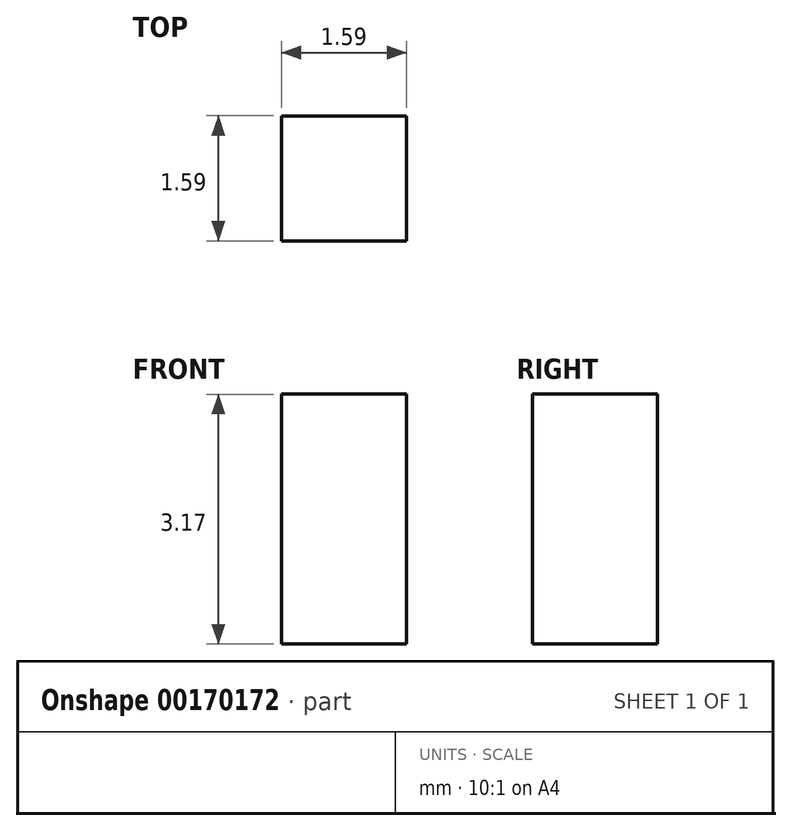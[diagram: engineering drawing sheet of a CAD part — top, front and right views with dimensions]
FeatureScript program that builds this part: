
annotation { "Feature Type Name" : "Feature", "Feature Type Description" : "" }
export const myFeature = defineFeature(function(context is Context, id is Id, definition is map)
    precondition{}
    {
        {
            var Q0;
            Q0=qCreatedBy(makeId("Top.planeOp"),FACE);
            var sketch = newSketch(context, id + "F0", { "sketchPlane" : qUnion([Q0])});
            skCircle(sketch, "E0.cCircle", {"center": v(0, 0) * mm, "radius": 29.07 * mm, "construction": true});
            skLineSegment(sketch, "E0.0", {"start": v(44.45, -29.08) * mm, "end": v(0, -29.07) * mm});
            skLineSegment(sketch, "E0.1", {"start": v(-44.45, -29.06) * mm, "end": v(0, 72.53) * mm});
            skLineSegment(sketch, "E0.2", {"start": v(0, 72.53) * mm, "end": v(44.45, -29.08) * mm});
            skPoint(sketch, "E0.0.midPoint", {"position": v(0, -29.07) * mm});
            skLineSegment(sketch, "E1.0", {"start": v(0, 50.35) * mm, "end": v(30.86, -20.19) * mm});
            skLineSegment(sketch, "E1.1", {"start": v(-30.86, -20.18) * mm, "end": v(0, 50.35) * mm});
            skLineSegment(sketch, "E1.2", {"start": v(30.86, -20.19) * mm, "end": v(-30.86, -20.18) * mm});
            skLineSegment(sketch, "E2", {"start": v(0, 14.54) * mm, "end": v(0, -29.07) * mm});
            skCircle(sketch, "E3", {"center": v(0, -24.63) * mm, "radius": 1.84 * mm});
            skLineSegment(sketch, "E4.bottom", {"start": v(-1.59, -20.18) * mm, "end": v(1.59, -20.18) * mm});
            skLineSegment(sketch, "E4.top", {"start": v(-1.59, -21.77) * mm, "end": v(1.59, -21.77) * mm});
            skLineSegment(sketch, "E4.left", {"start": v(-1.59, -20.18) * mm, "end": v(-1.59, -21.77) * mm});
            skLineSegment(sketch, "E4.right", {"start": v(1.59, -20.18) * mm, "end": v(1.59, -21.77) * mm});
            skLineSegment(sketch, "E5.top", {"start": v(-1.59, -27.48) * mm, "end": v(1.59, -27.48) * mm});
            skLineSegment(sketch, "E5.left", {"start": v(-1.59, -29.07) * mm, "end": v(-1.59, -27.48) * mm});
            skPoint(sketch, "E6", {"position": v(17.59, 10.15) * mm});
            skLineSegment(sketch, "E7.1.0", {"start": v(18.27, 8.72) * mm, "end": v(19.65, 9.5) * mm});
            skLineSegment(sketch, "E7.1.1", {"start": v(19.65, 9.5) * mm, "end": v(18.06, 12.26) * mm});
            skLineSegment(sketch, "E7.1.2", {"start": v(16.95, 11.62) * mm, "end": v(18.06, 12.26) * mm});
            skCircle(sketch, "E7.1.3", {"center": v(21.33, 12.31) * mm, "radius": 1.84 * mm});
            skLineSegment(sketch, "E7.1.4", {"start": v(24.6, 12.37) * mm, "end": v(23, 15.12) * mm});
            skLineSegment(sketch, "E7.1.5", {"start": v(25.97, 13.16) * mm, "end": v(24.6, 12.37) * mm});
            skLineSegment(sketch, "E7.1.6", {"start": v(24.38, 15.91) * mm, "end": v(23, 15.12) * mm});
            skLineSegment(sketch, "E7.1.7", {"start": v(25.97, 13.16) * mm, "end": v(24.38, 15.91) * mm});
            skLineSegment(sketch, "E7.1.8", {"start": v(18.27, 8.72) * mm, "end": v(18.04, 9.11) * mm});
            skLineSegment(sketch, "E7.2.0", {"start": v(-16.95, 11.62) * mm, "end": v(-18.06, 12.26) * mm});
            skLineSegment(sketch, "E7.2.1", {"start": v(-18.06, 12.26) * mm, "end": v(-19.65, 9.5) * mm});
            skLineSegment(sketch, "E7.2.2", {"start": v(-18.27, 8.72) * mm, "end": v(-19.65, 9.5) * mm});
            skCircle(sketch, "E7.2.3", {"center": v(-21.33, 12.31) * mm, "radius": 1.84 * mm});
            skLineSegment(sketch, "E7.2.4", {"start": v(-23, 15.12) * mm, "end": v(-24.6, 12.37) * mm});
            skLineSegment(sketch, "E7.2.5", {"start": v(-24.38, 15.91) * mm, "end": v(-23, 15.12) * mm});
            skLineSegment(sketch, "E7.2.6", {"start": v(-25.97, 13.16) * mm, "end": v(-24.6, 12.37) * mm});
            skLineSegment(sketch, "E7.2.7", {"start": v(-24.38, 15.91) * mm, "end": v(-25.97, 13.16) * mm});
            skLineSegment(sketch, "E7.2.8", {"start": v(-18.04, 9.12) * mm, "end": v(-18.27, 8.72) * mm});
            skCircle(sketch, "E8", {"center": v(0, 55.96) * mm, "radius": 1.84 * mm});
            skLineSegment(sketch, "E9.bottom", {"start": v(-1.59, 60.4) * mm, "end": v(1.59, 60.4) * mm});
            skLineSegment(sketch, "E9.top", {"start": v(-1.59, 58.81) * mm, "end": v(1.59, 58.81) * mm});
            skLineSegment(sketch, "E9.left", {"start": v(-1.59, 60.4) * mm, "end": v(-1.59, 58.81) * mm});
            skLineSegment(sketch, "E10.top", {"start": v(-1.59, 53.1) * mm, "end": v(1.59, 53.1) * mm});
            skLineSegment(sketch, "E10.left", {"start": v(-1.59, 51.51) * mm, "end": v(-1.59, 53.1) * mm});
            skLineSegment(sketch, "E10.right", {"start": v(1.59, 51.51) * mm, "end": v(1.59, 53.1) * mm});
            skLineSegment(sketch, "E11", {"start": v(1.59, 60.4) * mm, "end": v(1.59, 58.81) * mm});
            skLineSegment(sketch, "E12", {"start": v(-1.59, 51.51) * mm, "end": v(1.59, 51.51) * mm});
            skLineSegment(sketch, "E13.1.0", {"start": v(-14.02, 33.37) * mm, "end": v(-12.64, 34.16) * mm});
            skLineSegment(sketch, "E13.1.1", {"start": v(-12.64, 34.16) * mm, "end": v(-14.23, 36.91) * mm});
            skLineSegment(sketch, "E13.1.2", {"start": v(-15.6, 36.12) * mm, "end": v(-14.23, 36.91) * mm});
            skLineSegment(sketch, "E13.1.3", {"start": v(-14.02, 33.37) * mm, "end": v(-15.6, 36.12) * mm});
            skCircle(sketch, "E13.1.4", {"center": v(-10.96, 36.97) * mm, "radius": 1.84 * mm});
            skLineSegment(sketch, "E13.1.5", {"start": v(-7.7, 37.02) * mm, "end": v(-9.28, 39.77) * mm});
            skLineSegment(sketch, "E13.1.6", {"start": v(-6.32, 37.81) * mm, "end": v(-7.9, 40.56) * mm});
            skLineSegment(sketch, "E13.1.7", {"start": v(-6.32, 37.81) * mm, "end": v(-7.7, 37.02) * mm});
            skLineSegment(sketch, "E13.1.8", {"start": v(-7.9, 40.56) * mm, "end": v(-9.28, 39.77) * mm});
            skLineSegment(sketch, "E13.2.0", {"start": v(15.6, 36.12) * mm, "end": v(14.23, 36.92) * mm});
            skLineSegment(sketch, "E13.2.1", {"start": v(14.23, 36.92) * mm, "end": v(12.64, 34.17) * mm});
            skLineSegment(sketch, "E13.2.2", {"start": v(14.02, 33.37) * mm, "end": v(12.64, 34.17) * mm});
            skLineSegment(sketch, "E13.2.3", {"start": v(15.6, 36.12) * mm, "end": v(14.02, 33.37) * mm});
            skCircle(sketch, "E13.2.4", {"center": v(10.96, 36.97) * mm, "radius": 1.84 * mm});
            skLineSegment(sketch, "E13.2.5", {"start": v(9.28, 39.77) * mm, "end": v(7.7, 37.02) * mm});
            skLineSegment(sketch, "E13.2.6", {"start": v(7.9, 40.57) * mm, "end": v(6.32, 37.82) * mm});
            skLineSegment(sketch, "E13.2.7", {"start": v(7.9, 40.57) * mm, "end": v(9.28, 39.77) * mm});
            skLineSegment(sketch, "E13.2.8", {"start": v(6.32, 37.82) * mm, "end": v(7.7, 37.02) * mm});
            skPoint(sketch, "E13.center", {"position": v(0, 43.3) * mm});
            skLineSegment(sketch, "E14.bottom", {"start": v(-37.97, -16.32) * mm, "end": v(-32.89, -16.32) * mm});
            skLineSegment(sketch, "E14.top", {"start": v(-37.97, -18.15) * mm, "end": v(-32.89, -18.15) * mm});
            skLineSegment(sketch, "E14.left", {"start": v(-37.97, -16.32) * mm, "end": v(-37.97, -18.15) * mm});
            skLineSegment(sketch, "E14.right", {"start": v(-32.89, -16.32) * mm, "end": v(-32.89, -18.15) * mm});
            skLineSegment(sketch, "E15.bottom", {"start": v(-37.97, -25.26) * mm, "end": v(-32.89, -25.26) * mm});
            skLineSegment(sketch, "E15.top", {"start": v(-37.97, -27.1) * mm, "end": v(-32.89, -27.1) * mm});
            skLineSegment(sketch, "E15.left", {"start": v(-37.97, -25.26) * mm, "end": v(-37.97, -27.1) * mm});
            skLineSegment(sketch, "E15.right", {"start": v(-32.89, -25.26) * mm, "end": v(-32.89, -27.1) * mm});
            skLineSegment(sketch, "E16.MirrorCS", {"start": v(37.97, -16.32) * mm, "end": v(32.89, -16.32) * mm});
            skLineSegment(sketch, "E17.MirrorCS", {"start": v(37.97, -16.32) * mm, "end": v(37.97, -18.15) * mm});
            skLineSegment(sketch, "E18.MirrorCS", {"start": v(32.89, -16.32) * mm, "end": v(32.89, -18.15) * mm});
            skLineSegment(sketch, "E19.MirrorCS", {"start": v(37.97, -18.15) * mm, "end": v(32.89, -18.15) * mm});
            skLineSegment(sketch, "E20.MirrorCS", {"start": v(37.97, -25.26) * mm, "end": v(32.89, -25.26) * mm});
            skLineSegment(sketch, "E21.MirrorCS", {"start": v(37.97, -25.26) * mm, "end": v(37.97, -27.1) * mm});
            skLineSegment(sketch, "E22.MirrorCS", {"start": v(37.97, -27.1) * mm, "end": v(32.89, -27.1) * mm});
            skLineSegment(sketch, "E23.MirrorCS", {"start": v(32.89, -25.26) * mm, "end": v(32.89, -27.1) * mm});
            skPoint(sketch, "E24.orphan", {"position": v(-16.68, 11.47) * mm});
            skPoint(sketch, "E25.orphan", {"position": v(16.68, 11.47) * mm});
            skLineSegment(sketch, "E26.trimOffspring", {"start": v(-1.59, -29.07) * mm, "end": v(-44.45, -29.06) * mm});
            skLineSegment(sketch, "E27", {"start": v(1.59, -27.48) * mm, "end": v(1.59, -29.07) * mm});
            skLineSegment(sketch, "E28", {"start": v(1.59, -29.07) * mm, "end": v(-1.59, -29.07) * mm});
            skSolve(sketch);
        }
        {
            var Q0;
            Q0=makeQuery(id+"F0.imprint","IMPRINT",FACE,{"disambiguationData":[TD([[makeQuery(id+"F0.imprint","IMPRINT",EDGE,{"derivedFrom":sQuery(id+"F0.wireOp",EDGE,"E0.0")}),-1.0]])]});
            extrude(context, id + "F1", {"entities" : qUnion([Q0]), "depth" : 3.17 * mm});
        }
    });
